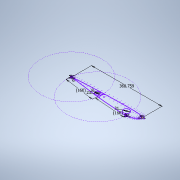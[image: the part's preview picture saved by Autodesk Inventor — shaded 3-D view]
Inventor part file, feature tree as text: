
AUTODESK INVENTOR PART (.ipt)
format: ipt  version: 2022 (Build 260153000, 153)  size: 146,432 bytes
history: native  units: mm
features: sketch x1
ambient origin geometry x8: Origin, YZ Plane, XZ Plane, XY Plane, X Axis, Y Axis, Z Axis, Center Point
feature tree (1):
  sketch  "Sketch1"  dims[d5=160.0mm d8=160.0mm d17=5.0mm d18=5.0mm d25=6.0mm d26=5.0mm d27=5.0mm d31=34.456mm d36=5.0mm d37=5.0mm d41=23.0mm d50=368.759386mm d60=8.0mm d62=31.0mm]
